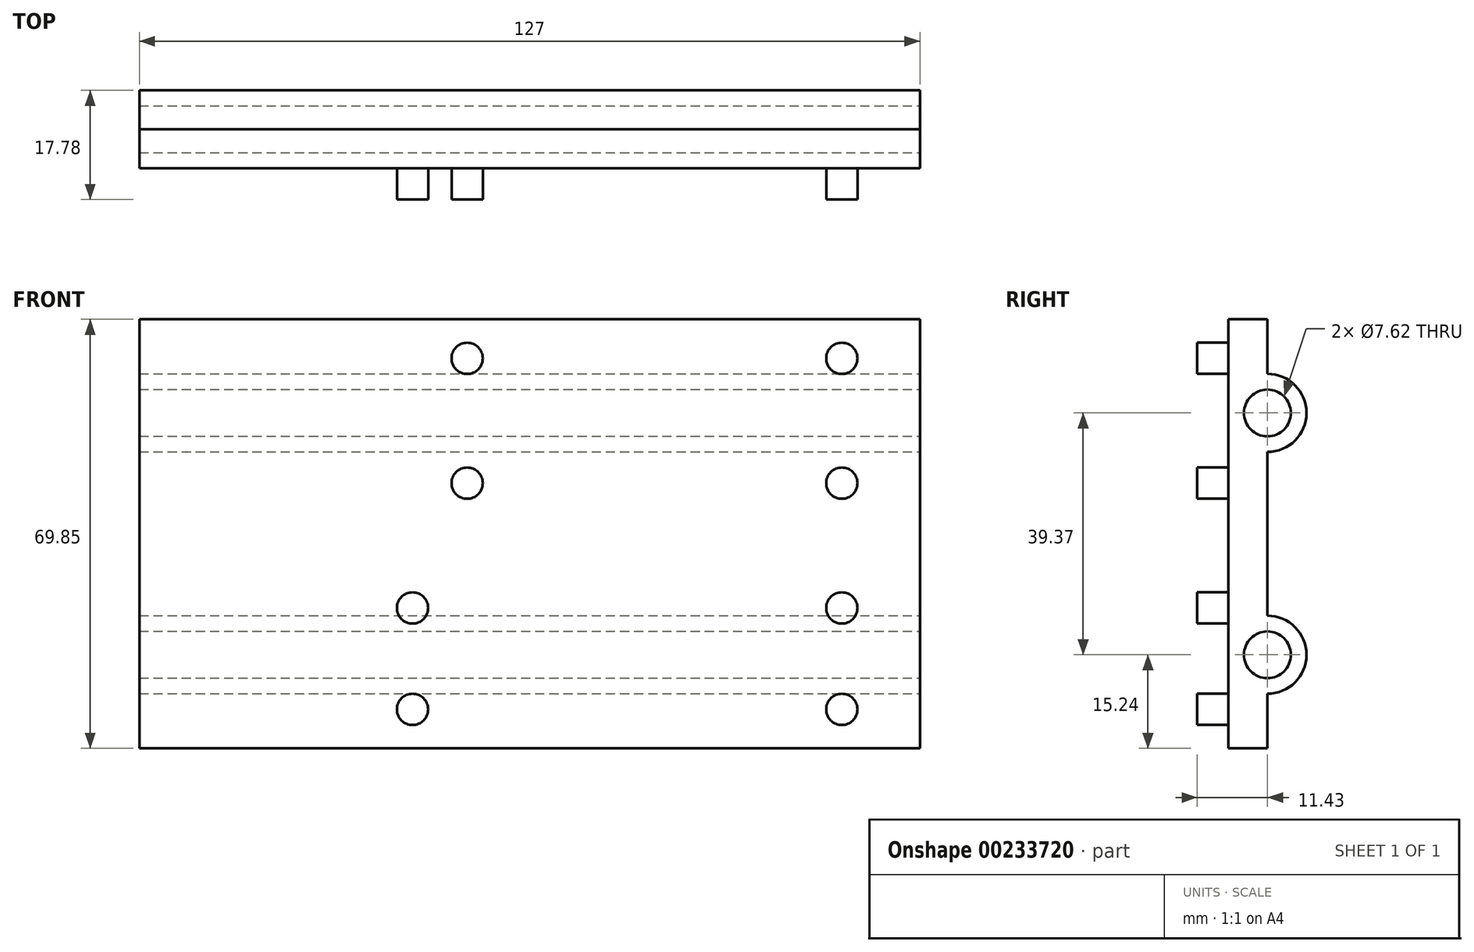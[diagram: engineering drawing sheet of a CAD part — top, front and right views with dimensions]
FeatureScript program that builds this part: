
annotation { "Feature Type Name" : "Feature", "Feature Type Description" : "" }
export const myFeature = defineFeature(function(context is Context, id is Id, definition is map)
    precondition{}
    {
        {
            var Q0;
            Q0=qCreatedBy(makeId("Front.planeOp"),FACE);
            var sketch = newSketch(context, id + "F6", { "sketchPlane" : qUnion([Q0])});
            skLineSegment(sketch, "E0.bottom", {"start": v(-95.6, 69.85) * mm, "end": v(31.4, 69.85) * mm});
            skLineSegment(sketch, "E0.top", {"start": v(-95.6, 0) * mm, "end": v(31.4, 0) * mm});
            skLineSegment(sketch, "E0.left", {"start": v(-95.6, 69.85) * mm, "end": v(-95.6, 0) * mm});
            skLineSegment(sketch, "E0.right", {"start": v(31.4, 69.85) * mm, "end": v(31.4, 0) * mm});
            skSolve(sketch);
        }
        {
            var Q0;
            Q0=makeQuery(id+"F6.imprint","IMPRINT",FACE,{"disambiguationData":[TD([[makeQuery(id+"F6.imprint","IMPRINT",EDGE,{"derivedFrom":sQuery(id+"F6.wireOp",EDGE,"E0.bottom")}),-1.0]])]});
            extrude(context, id + "F0", {"entities" : qUnion([Q0]), "depth" : 6.35 * mm});
        }
        {
            var Q0;
            Q0=makeQuery(id+"F0.opExtrude","SWEPT_FACE",FACE,{"disambiguationData":[OSD([sQuery(id+"F6.wireOp",EDGE,"E0.right")])]});
            var sketch = newSketch(context, id + "F1", { "sketchPlane" : qUnion([Q0])});
            skCircle(sketch, "E1", {"center": v(0, 54.6) * mm, "radius": 6.35 * mm});
            skCircle(sketch, "E2", {"center": v(0, 15.24) * mm, "radius": 6.35 * mm});
            skSolve(sketch);
        }
        {
            var Q0;
            Q0 = qSketchRegion(id + "F1", true);
            extrude(context, id + "F2", {"entities" : qUnion([Q0]), "operationType" : NewBodyOperationType.ADD, "oppositeDirection" : true, "depth" : 127 * mm});
        }
        {
            var Q0;
            Q0=makeQuery(id+"F2.boolean.opBoolean","MERGE",FACE,{"derivedFrom":[makeQuery(id+"F0.opExtrude","SWEPT_FACE",FACE,{"disambiguationData":[OSD([sQuery(id+"F6.wireOp",EDGE,"E0.right")])]}),makeQuery(id+"F2.opExtrude","CAP_FACE",FACE,{"disambiguationData":[OSD([sQuery(id+"F1.wireOp",EDGE,"E1")])],"isStart":true}),makeQuery(id+"F2.opExtrude","CAP_FACE",FACE,{"disambiguationData":[OSD([sQuery(id+"F1.wireOp",EDGE,"E2")])],"isStart":true})]});
            var sketch = newSketch(context, id + "F7", { "sketchPlane" : qUnion([Q0])});
            skCircle(sketch, "E3", {"center": v(0, 54.6) * mm, "radius": 3.81 * mm});
            skCircle(sketch, "E4", {"center": v(0, 15.24) * mm, "radius": 3.81 * mm});
            skSolve(sketch);
        }
        {
            var Q0;
            Q0 = qSketchRegion(id + "F7", true);
            extrude(context, id + "F8", {"entities" : qUnion([Q0]), "operationType" : NewBodyOperationType.REMOVE, "oppositeDirection" : true, "depth" : 127 * mm});
        }
        {
            var Q0;
            Q0=makeQuery(id+"F0.opExtrude","CAP_FACE",FACE,{"disambiguationData":[OSD([sQuery(id+"F6.wireOp",EDGE,"E0.bottom"),sQuery(id+"F6.wireOp",EDGE,"E0.top"),sQuery(id+"F6.wireOp",EDGE,"E0.left"),sQuery(id+"F6.wireOp",EDGE,"E0.right")])],"isStart":false});
            var sketch = newSketch(context, id + "F3", { "sketchPlane" : qUnion([Q0])});
            skCircle(sketch, "E5", {"center": v(-51.16, 6.35) * mm, "radius": 2.54 * mm});
            skCircle(sketch, "E6.0.1.0", {"center": v(-51.16, 22.86) * mm, "radius": 2.54 * mm});
            skCircle(sketch, "E6.1.0.0", {"center": v(18.7, 6.35) * mm, "radius": 2.54 * mm});
            skCircle(sketch, "E6.1.1.0", {"center": v(18.7, 22.86) * mm, "radius": 2.54 * mm});
            skLineSegment(sketch, "E6.direction1", {"start": v(-51.16, 6.35) * mm, "end": v(18.7, 6.35) * mm, "construction": true});
            skLineSegment(sketch, "E6.direction2", {"start": v(-51.16, 6.35) * mm, "end": v(-51.16, 22.86) * mm, "construction": true});
            skSolve(sketch);
        }
        {
            var Q0;
            Q0 = qSketchRegion(id + "F3", true);
            extrude(context, id + "F4", {"entities" : qUnion([Q0]), "operationType" : NewBodyOperationType.ADD, "depth" : 5.08 * mm});
        }
        {
            var Q0;
            Q0=makeQuery(id+"F0.opExtrude","CAP_FACE",FACE,{"disambiguationData":[OSD([sQuery(id+"F6.wireOp",EDGE,"E0.bottom"),sQuery(id+"F6.wireOp",EDGE,"E0.top"),sQuery(id+"F6.wireOp",EDGE,"E0.left"),sQuery(id+"F6.wireOp",EDGE,"E0.right")])],"isStart":false});
            var sketch = newSketch(context, id + "F9", { "sketchPlane" : qUnion([Q0])});
            skCircle(sketch, "E7", {"center": v(-42.27, 43.18) * mm, "radius": 2.54 * mm});
            skCircle(sketch, "E8.0.1.0", {"center": v(-42.27, 63.5) * mm, "radius": 2.54 * mm});
            skCircle(sketch, "E8.1.0.0", {"center": v(18.7, 43.18) * mm, "radius": 2.54 * mm});
            skCircle(sketch, "E8.1.1.0", {"center": v(18.7, 63.5) * mm, "radius": 2.54 * mm});
            skLineSegment(sketch, "E8.direction1", {"start": v(-42.27, 43.18) * mm, "end": v(18.7, 43.18) * mm, "construction": true});
            skLineSegment(sketch, "E8.direction2", {"start": v(-42.27, 43.18) * mm, "end": v(-42.27, 63.5) * mm, "construction": true});
            skSolve(sketch);
        }
        {
            var Q0;
            Q0 = qSketchRegion(id + "F9", true);
            extrude(context, id + "F5", {"entities" : qUnion([Q0]), "operationType" : NewBodyOperationType.ADD, "depth" : 5.08 * mm});
        }
    });
